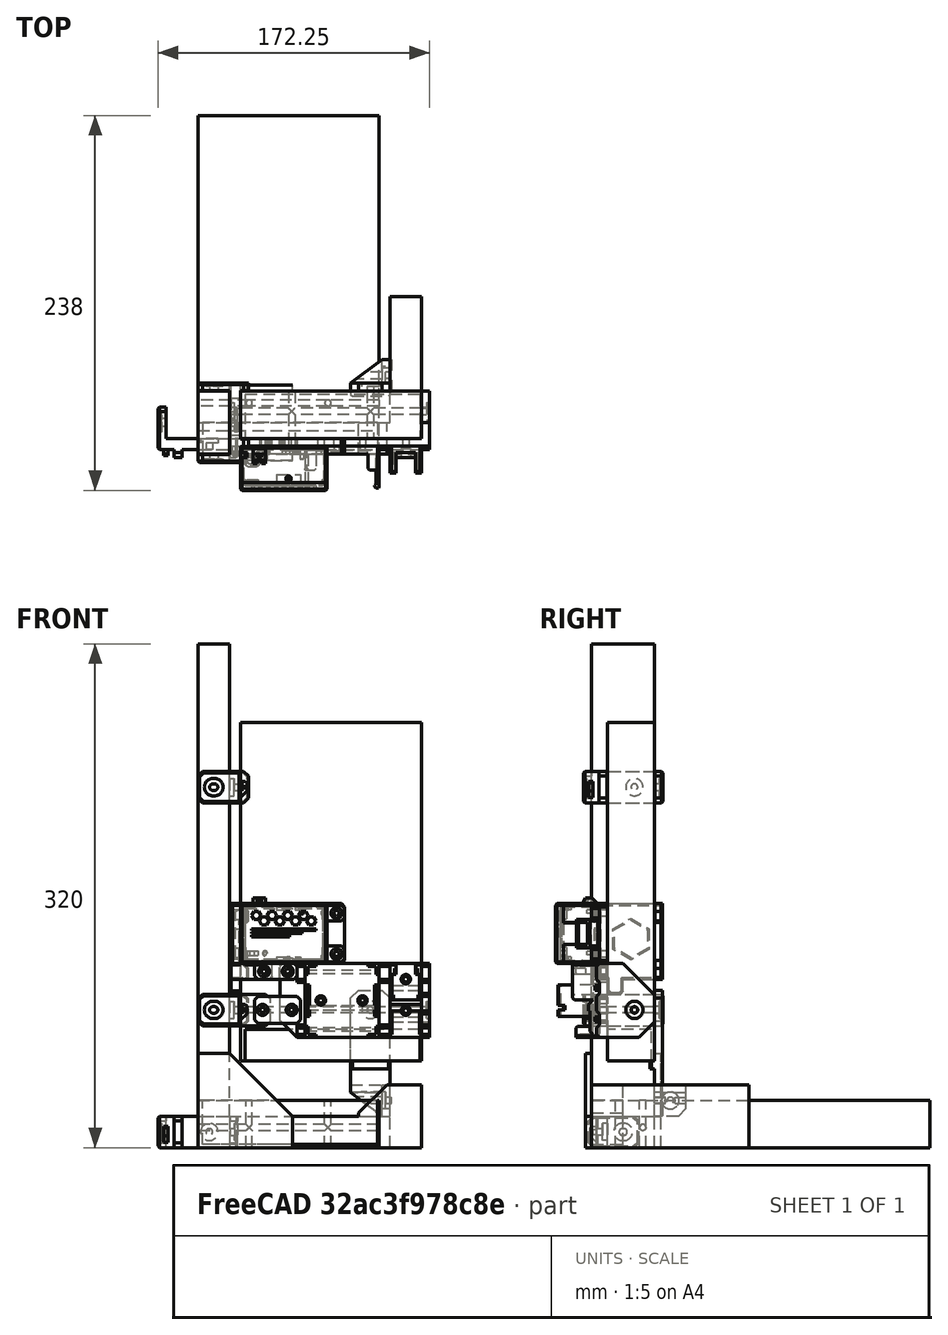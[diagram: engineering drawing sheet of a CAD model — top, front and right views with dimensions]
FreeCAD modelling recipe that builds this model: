
FCSTD DOCUMENT  (FreeCAD 0.18R16146 (Git))
Label: psu-aio-mount
License: All rights reserved
LicenseURL: http://en.wikipedia.org/wiki/All_rights_reserved
objects: Part::Box×50, Part::Chamfer×33, Part::Cylinder×32, Part::MultiFuse×30, Part::Feature×16, Part::Cut×16
note: 177 computed .brp shape members not serialized (recipe doc carries the construction recipe); baked Part::Feature solids carry a one-line shape summary decoded from their .brp

FEATURE [Part::Box] Box  label="Cube"
  AttacherType = Attacher::AttachEngine3D
  Height = 60
  Length = 60
  Width = 4
FEATURE [Part::Chamfer] Chamfer
  Base = -> Box
  Edges = 1 edges r=40: [Edge6]
  Placement = pos=(0,-4,0) rot=(0,0,1;0rad)
FEATURE [Part::Box] Box001  label="Cube001"
  AttacherType = Attacher::AttachEngine3D
  Height = 20
  Length = 122
  Width = 40
FEATURE [Part::Box] Box002  label="Cube002"
  AttacherType = Attacher::AttachEngine3D
  Height = 300
  Length = 20
  Placement = pos=(0,0,20) rot=(0,0,1;0rad)
  Width = 40
FEATURE [Part::Box] Box003  label="Cube003"
  AttacherType = Attacher::AttachEngine3D
  Height = 40
  Length = 20
  Placement = pos=(122,0,0) rot=(0,0,1;0rad)
  Width = 100
FEATURE [Part::Feature] Chamfer001
  Placement = pos=(0,40,0) rot=(0,0,1;0rad)
  shape: bbox 60 x 4 x 60 mm, 7 faces (baked)
FEATURE [Part::Box] Box004  label="Cube004"
  AttacherType = Attacher::AttachEngine3D
  Height = 20
  Length = 20
  Placement = pos=(102,0,20) rot=(0,0,1;0rad)
  Width = 20
FEATURE [Part::Chamfer] Chamfer002
  Base = -> Box004
  Edges = 1 edges r=18: [Edge2]
FEATURE [Part::MultiFuse] Fusion  label="Frame-pred"
  Shapes = -> [Chamfer002,Box001,Chamfer001,Box003,Box002,Chamfer]
FEATURE [Part::Feature] Cut002001  label="PSU-pref"
  Placement = pos=(142,40,55) rot=(0.57735,-0.57735,0.57735;2.0944rad)
  shape: bbox 115 x 30 x 215 mm, 17 faces (baked)
FEATURE [Part::Feature] Cut001001  label="sonoff-mounter001"
  Placement = pos=(130,8,117) rot=(0.57735,0.57735,-0.57735;2.0944rad)
  shape: bbox 47 x 26.5 x 47 mm, 92 faces (baked)
FEATURE [Part::Feature] Chamfer003001001  label="plug-holder-2-pin"
  Placement = pos=(122,5,117) rot=(0.57735,0.57735,-0.57735;2.0944rad)
  shape: bbox 20 x 17 x 47 mm, 63 faces (baked)
FEATURE [Part::Box] Box006  label="Cube006"
  AttacherType = Attacher::AttachEngine3D
  Height = 20
  Length = 40.5
  Placement = pos=(-20.25,3,0) rot=(0,0,1;0rad)
  Width = 7
FEATURE [Part::Box] Box007  label="Cube007"
  AttacherType = Attacher::AttachEngine3D
  Height = 20
  Length = 5
  Placement = pos=(-25.25,3,0) rot=(0,0,1;0rad)
  Width = 27
FEATURE [Part::Box] Box008  label="Cube008"
  AttacherType = Attacher::AttachEngine3D
  Height = 20
  Length = 5
  Placement = pos=(20.25,3,0) rot=(0,0,1;0rad)
  Width = 27
FEATURE [Part::Box] Box009  label="Cube009"
  AttacherType = Attacher::AttachEngine3D
  Height = 20
  Length = 5
  Placement = pos=(20.25,-2,0) rot=(0,0,1;0rad)
  Width = 5
FEATURE [Part::Box] Box010  label="Cube010"
  AttacherType = Attacher::AttachEngine3D
  Height = 20
  Length = 5
  Placement = pos=(-15.25,-2,0) rot=(0,0,1;0rad)
  Width = 5
FEATURE [Part::Cylinder] Cylinder
  Angle = 360
  AttacherType = Attacher::AttachEngine3D
  Height = 10
  Placement = pos=(7.2,11,10) rot=(1,0,0;1.5708rad)
  Radius = 2.1
FEATURE [Part::Cylinder] Cylinder001
  Angle = 360
  AttacherType = Attacher::AttachEngine3D
  Height = 10
  Placement = pos=(-20,20,10) rot=(0,-1,0;1.5708rad)
  Radius = 2.1
FEATURE [Part::Cylinder] Cylinder002
  Angle = 360
  AttacherType = Attacher::AttachEngine3D
  Height = 10
  Placement = pos=(30,20,10) rot=(0,-1,0;1.5708rad)
  Radius = 2.1
FEATURE [Part::Cylinder] Cylinder003
  Angle = 360
  AttacherType = Attacher::AttachEngine3D
  Height = 3
  Placement = pos=(7.2,10,10) rot=(1,0,0;1.5708rad)
  Radius = 5.5
FEATURE [Part::MultiFuse] Fusion001
  Shapes = -> [Cylinder003,Cylinder]
FEATURE [Part::Cylinder] Cylinder004
  Angle = 360
  AttacherType = Attacher::AttachEngine3D
  Height = 2
  Placement = pos=(25.25,20,10) rot=(0,-1,0;1.5708rad)
  Radius = 5.5
FEATURE [Part::MultiFuse] Fusion002
  Shapes = -> [Cylinder004,Cylinder002]
FEATURE [Part::Cylinder] Cylinder005
  Angle = 360
  AttacherType = Attacher::AttachEngine3D
  Height = 2
  Placement = pos=(-23.25,20,10) rot=(0,-1,0;1.5708rad)
  Radius = 5.5
FEATURE [Part::MultiFuse] Fusion003
  Shapes = -> [Cylinder005,Cylinder001]
FEATURE [Part::MultiFuse] Fusion004
  Shapes = -> [Box010,Box008,Box007,Box006,Box009]
FEATURE [Part::Feature] Fusion003001  label="Fusion005"
  Placement = pos=(0,1,0) rot=(0,0,1;0rad)
  shape: bbox 10 x 11 x 11 mm, 7 faces (baked)
FEATURE [Part::Feature] Fusion002001  label="Fusion006"
  Placement = pos=(0,1,0) rot=(0,0,1;0rad)
  shape: bbox 10 x 11 x 11 mm, 7 faces (baked)
FEATURE [Part::Box] Box011  label="Cube011"
  AttacherType = Attacher::AttachEngine3D
  Height = 4.2
  Length = 9
  Placement = pos=(-26,20,7.9) rot=(0,0,1;0rad)
  Width = 1
FEATURE [Part::Box] Box012  label="Cube012"
  AttacherType = Attacher::AttachEngine3D
  Height = 4.2
  Length = 9
  Placement = pos=(19,20,7.9) rot=(0,0,1;0rad)
  Width = 1
FEATURE [Part::Box] Box013  label="Cube013"
  AttacherType = Attacher::AttachEngine3D
  Height = 11
  Length = 2
  Placement = pos=(-25.25,20,4.5) rot=(0,0,1;0rad)
  Width = 1
FEATURE [Part::Box] Box014  label="Cube014"
  AttacherType = Attacher::AttachEngine3D
  Height = 11
  Length = 2
  Placement = pos=(23.25,20,4.5) rot=(0,0,1;0rad)
  Width = 1
FEATURE [Part::MultiFuse] Fusion003002
  Placement = pos=(0,-0.5,0) rot=(0,0,1;0rad)
  Shapes = -> [Box013,Box014,Box012,Box011,Fusion002001,Fusion003001,Fusion002,Fusion003]
FEATURE [Part::Cut] Cut
  Base = -> Fusion004
  Tool = -> Fusion003002
FEATURE [Part::Cut] Cut003023001003
  Base = -> Cut
  Tool = -> Fusion001
FEATURE [Part::Chamfer] Chamfer003001002
  Base = -> Cut003023001003
  Edges = 8 edges r=3: [Edge14,Edge18,Edge54,Edge57,Edge69,Edge75,Edge80,Edge93]
FEATURE [Part::Box] Box015  label="Cube015"
  AttacherType = Attacher::AttachEngine3D
  Height = 3
  Length = 3
  Placement = pos=(-22,1,8.5) rot=(0,0,1;0rad)
  Width = 3
FEATURE [Part::Box] Box016  label="Cube016"
  AttacherType = Attacher::AttachEngine3D
  Height = 10
  Length = 3
  Placement = pos=(-22,-1,3.5) rot=(0,0,1;0rad)
  Width = 5
FEATURE [Part::Chamfer] Chamfer003001003
  Base = -> Box016
  Edges = 1 edges r=4: [Edge9]
FEATURE [Part::Cut] Cut003023001004
  Base = -> Chamfer003001003
  Tool = -> Box015
FEATURE [Part::Chamfer] Chamfer003001004
  Base = -> Cut003023001004
  Edges = 1 edges r=1: [Edge12]
FEATURE [Part::MultiFuse] Fusion003003
  Shapes = -> [Chamfer003001002,Chamfer003001004]
FEATURE [Part::Chamfer] Chamfer003001005  label="PSU-mounter"
  Base = -> Fusion003003
  Edges = 16 edges r=1: [Edge13,Edge16,Edge21,Edge25,Edge27,Edge47,Edge65,Edge76,Edge95,Edge96,Edge97,Edge110,Edge116,Edge119,Edge120,Edge139]
FEATURE [Part::Box] Box017  label="Cube017"
  AttacherType = Attacher::AttachEngine3D
  Height = 30
  Length = 115
  Placement = pos=(0,15,0) rot=(0,0,1;0rad)
  Width = 5
FEATURE [Part::Cylinder] Cylinder006
  Angle = 360
  AttacherType = Attacher::AttachEngine3D
  Height = 41
  Placement = pos=(32.5,32.5,0) rot=(0,0,1;0rad)
  Radius = 2.1
FEATURE [Part::Box] Box018  label="Cube018"
  AttacherType = Attacher::AttachEngine3D
  Height = 5
  Length = 95
  Placement = pos=(25,15,30) rot=(0,0,1;0rad)
  Width = 47
FEATURE [Part::Box] Box019  label="Cube019"
  AttacherType = Attacher::AttachEngine3D
  Height = 35
  Length = 5
  Placement = pos=(115,15,0) rot=(0,0,1;0rad)
  Width = 47
FEATURE [Part::Box] Box020  label="Cube020"
  AttacherType = Attacher::AttachEngine3D
  Height = 3
  Length = 5
  Placement = pos=(115,15,35) rot=(0,0,1;0rad)
  Width = 8
FEATURE [Part::Box] Box021  label="Cube021"
  AttacherType = Attacher::AttachEngine3D
  Height = 3
  Length = 5
  Placement = pos=(115,30,35) rot=(0,0,1;0rad)
  Width = 13
FEATURE [Part::Box] Box022  label="Cube022"
  AttacherType = Attacher::AttachEngine3D
  Height = 3
  Length = 5
  Placement = pos=(115,50,35) rot=(0,0,1;0rad)
  Width = 12
FEATURE [Part::Box] Box023  label="Cube023"
  AttacherType = Attacher::AttachEngine3D
  Height = 3
  Length = 7
  Placement = pos=(88,15,35) rot=(0,0,1;0rad)
  Width = 8
FEATURE [Part::Box] Box024  label="Cube024"
  AttacherType = Attacher::AttachEngine3D
  Height = 3
  Length = 7
  Placement = pos=(88,50,35) rot=(0,0,1;0rad)
  Width = 12
FEATURE [Part::Box] Box025  label="Cube025"
  AttacherType = Attacher::AttachEngine3D
  Height = 3
  Length = 5
  Placement = pos=(36,50,35) rot=(0,0,1;0rad)
  Width = 12
FEATURE [Part::Box] Box026  label="Cube026"
  AttacherType = Attacher::AttachEngine3D
  Height = 3
  Length = 5
  Placement = pos=(36,15,35) rot=(0,0,1;0rad)
  Width = 8
FEATURE [Part::MultiFuse] Fusion003004
  Placement = pos=(0,0,-1) rot=(0,0,1;0rad)
  Shapes = -> [Box020,Box021,Box022,Box023,Box024,Box025,Box026]
FEATURE [Part::Chamfer] Chamfer003001007
  Base = -> Fusion003004
  Edges = 14 edges r=2: [Edge10,Edge12,Edge22,Edge24,Edge34,Edge36,Edge46,Edge48,Edge58,Edge60,Edge70,Edge72,Edge82,Edge84]
FEATURE [Part::Cylinder] Cylinder007
  Angle = 360
  AttacherType = Attacher::AttachEngine3D
  Height = 3
  Placement = pos=(32.5,32.5,32) rot=(0,0,1;0rad)
  Radius = 5.5
FEATURE [Part::MultiFuse] Fusion003005
  Shapes = -> [Box018,Box019,Chamfer003001007]
FEATURE [Part::Cylinder] Cylinder008
  Angle = 360
  AttacherType = Attacher::AttachEngine3D
  Height = 10
  Placement = pos=(114,32.5,12.8) rot=(0,1,0;1.5708rad)
  Radius = 2.1
FEATURE [Part::Cylinder] Cylinder009
  Angle = 360
  AttacherType = Attacher::AttachEngine3D
  Height = 2
  Placement = pos=(118,32.5,12.8) rot=(0,1,0;1.5708rad)
  Radius = 5.5
FEATURE [Part::MultiFuse] Fusion003007
  Shapes = -> [Cylinder009,Cylinder008]
FEATURE [Part::MultiFuse] Fusion003008
  Shapes = -> [Cylinder006,Cylinder007]
FEATURE [Part::MultiFuse] Fusion003009
  Shapes = -> [Fusion003007,Fusion003008]
FEATURE [Part::Cut] Cut003023001006
  Base = -> Fusion003005
  Tool = -> Fusion003009
FEATURE [Part::Chamfer] Chamfer003001008
  Base = -> Cut003023001006
  Edges = 1 edges r=10: [Edge115]
FEATURE [Part::Chamfer] Chamfer003001009
  Base = -> Chamfer003001008
  Edges = 1 edges r=20: [Edge16]
FEATURE [Part::Chamfer] Chamfer003001010
  Base = -> Chamfer003001009
  Edges = 1 edges r=10.99: [Edge44]
FEATURE [Part::Cylinder] Cylinder010
  Angle = 360
  AttacherType = Attacher::AttachEngine3D
  Height = 10
  Placement = pos=(51,38.5,29) rot=(0,0,1;0rad)
  Radius = 2.05
FEATURE [Part::Cylinder] Cylinder011
  Angle = 360
  AttacherType = Attacher::AttachEngine3D
  Height = 10
  Placement = pos=(77.5,38.5,29) rot=(0,0,1;0rad)
  Radius = 2.05
FEATURE [Part::Cylinder] Cylinder012
  Angle = 360
  AttacherType = Attacher::AttachEngine3D
  Height = 10
  Placement = pos=(105,52,29) rot=(0,0,1;0rad)
  Radius = 2.05
FEATURE [Part::Cylinder] Cylinder013
  Angle = 360
  AttacherType = Attacher::AttachEngine3D
  Height = 10
  Placement = pos=(105,32,29) rot=(0,0,1;0rad)
  Radius = 2.05
FEATURE [Part::MultiFuse] Fusion003010
  Shapes = -> [Cylinder013,Cylinder012,Cylinder011,Cylinder010]
FEATURE [Part::Cut] Cut003023001007
  Base = -> Chamfer003001010
  Tool = -> Fusion003010
FEATURE [Part::Cylinder] Cylinder014
  Angle = 360
  AttacherType = Attacher::AttachEngine3D
  Height = 10
  Placement = pos=(30,57,26.5) rot=(0,0,1;0rad)
  Radius = 2.1
FEATURE [Part::Chamfer] Chamfer003001011
  Base = -> Cut003023001007
  Edges = 1 edges r=2: [Edge13]
FEATURE [Part::Cut] Cut003023001008
  Base = -> Chamfer003001011
  Placement = pos=(27,40,55) rot=(1,0,0;1.5708rad)
  Tool = -> Cylinder014
FEATURE [Part::Feature] Chamfer003001005001  label="PSU-mounter001"
  Placement = pos=(30,20,77.5) rot=(0,0,1;1.5708rad)
  shape: bbox 32 x 50.5 x 20 mm, 102 faces (baked)
FEATURE [Part::Feature] Chamfer003001005002  label="PSU-mounter002"
  Placement = pos=(30,20,219) rot=(0,0,1;1.5708rad)
  shape: bbox 32 x 50.5 x 20 mm, 102 faces (baked)
FEATURE [Part::Feature] Cut002001001  label="PSU-pref001"
  Placement = pos=(115,-4e-15,-2.8e-14) rot=(0,0,1;1.5708rad)
  shape: bbox 115 x 215 x 30 mm, 17 faces (baked)
FEATURE [Part::Box] Box027  label="Cube027"
  AttacherType = Attacher::AttachEngine3D
  Height = 3
  Length = 25
  Placement = pos=(70,-5,0) rot=(0,0,1;0rad)
  Width = 5
FEATURE [Part::Cylinder] Cylinder015
  Angle = 360
  AttacherType = Attacher::AttachEngine3D
  Height = 32
  Placement = pos=(82.5,32.5,-15) rot=(0,0,1;0rad)
  Radius = 2.1
FEATURE [Part::Box] Box028  label="Cube028"
  AttacherType = Attacher::AttachEngine3D
  Height = 5
  Length = 25
  Placement = pos=(70,-15,-5) rot=(0,0,1;0rad)
  Width = 60
FEATURE [Part::Box] Box029  label="Cube029"
  AttacherType = Attacher::AttachEngine3D
  Height = 20
  Length = 5
  Placement = pos=(90,-35,-20) rot=(0,0,1;0rad)
  Width = 20
FEATURE [Part::Box] Box030  label="Cube030"
  AttacherType = Attacher::AttachEngine3D
  Height = 20
  Length = 25
  Placement = pos=(70,-20,-20) rot=(0,0,1;0rad)
  Width = 5
FEATURE [Part::Cylinder] Cylinder016
  Angle = 360
  AttacherType = Attacher::AttachEngine3D
  Height = 25
  Placement = pos=(95,-25,-10) rot=(0,-1,0;1.5708rad)
  Radius = 2.1
FEATURE [Part::Cylinder] Cylinder017
  Angle = 360
  AttacherType = Attacher::AttachEngine3D
  Height = 22
  Placement = pos=(92,-25,-10) rot=(0,-1,0;1.5708rad)
  Radius = 5.5
FEATURE [Part::MultiFuse] Fusion003011
  Shapes = -> [Cylinder017,Cylinder016]
FEATURE [Part::Box] Box031  label="Cube031"
  AttacherType = Attacher::AttachEngine3D
  Height = 5
  Length = 25
  Placement = pos=(70,-35,-5) rot=(0,0,1;0rad)
  Width = 20
FEATURE [Part::Chamfer] Chamfer003001005003
  Base = -> Box030
  Edges = 1 edges: [Edge4 r1=15 r2=20]
FEATURE [Part::Chamfer] Chamfer003001005004
  Base = -> Box031
  Edges = 1 edges: [Edge1 r1=15 r2=20]
FEATURE [Part::Box] Box032  label="Cube032"
  AttacherType = Attacher::AttachEngine3D
  Height = 7
  Length = 2
  Placement = pos=(94,-27,-20) rot=(0,0,1;0rad)
  Width = 4
FEATURE [Part::Box] Box033  label="Cube033"
  AttacherType = Attacher::AttachEngine3D
  Height = 7
  Length = 2
  Placement = pos=(94,-27,-7) rot=(0,0,1;0rad)
  Width = 4
FEATURE [Part::MultiFuse] Fusion003012
  Shapes = -> [Box033,Box032,Chamfer003001005004,Chamfer003001005003,Box029,Box028,Box027]
FEATURE [Part::Chamfer] Chamfer003001005005
  Base = -> Fusion003012
  Edges = 2 edges r=1: [Edge85,Edge92]
FEATURE [Part::Chamfer] Chamfer003001005006
  Base = -> Chamfer003001005005
  Edges = 1 edges r=5: [Edge90]
FEATURE [Part::Cut] Cut003023001009
  Base = -> Chamfer003001005006
  Tool = -> Fusion003011
FEATURE [Part::Chamfer] Chamfer003001005007
  Base = -> Cut003023001009
  Edges = 2 edges r=5: [Edge94,Edge113]
FEATURE [Part::Cylinder] Cylinder018
  Angle = 360
  AttacherType = Attacher::AttachEngine3D
  Height = 2
  Placement = pos=(82.5,32.5,-5) rot=(0,0,1;0rad)
  Radius = 5.5
FEATURE [Part::MultiFuse] Fusion003013
  Shapes = -> [Cylinder018,Cylinder015]
FEATURE [Part::Cut] Cut003023001010  label="psu-supporter"
  Base = -> Chamfer003001005007
  Placement = pos=(27,40,55) rot=(1,0,0;1.5708rad)
  Tool = -> Fusion003013
FEATURE [Part::Box] Box034  label="Cube034"
  AttacherType = Attacher::AttachEngine3D
  Height = 20.3
  Length = 18.15
  Placement = pos=(28,4.75,77.85) rot=(0,0,1;0rad)
  Width = 5
FEATURE [Part::Box] Box035  label="Cube035"
  AttacherType = Attacher::AttachEngine3D
  Height = 13
  Length = 13
  Placement = pos=(53,5,81) rot=(0,0,1;0rad)
  Width = 5
FEATURE [Part::MultiFuse] Fusion003015
  Shapes = -> [Cut003023001008,Box035]
FEATURE [Part::Cylinder] Cylinder019
  Angle = 360
  AttacherType = Attacher::AttachEngine3D
  Height = 10
  Placement = pos=(59.5,11,87.5) rot=(1,0,0;1.5708rad)
  Radius = 2.05
FEATURE [Part::Cylinder] Cylinder020
  Angle = 360
  AttacherType = Attacher::AttachEngine3D
  Height = 10
  Placement = pos=(41,10,87.5) rot=(1,0,0;1.5708rad)
  Radius = 2.05
FEATURE [Part::Box] Box036  label="Cube036"
  AttacherType = Attacher::AttachEngine3D
  Height = 20
  Length = 18
  Placement = pos=(28,4.75,78) rot=(0,0,1;0rad)
  Width = 5
FEATURE [Part::Chamfer] Chamfer003001005008
  Base = -> Box036
  Edges = 2 edges r=3: [Edge6,Edge8]
  Placement = pos=(0,0,-0.5) rot=(0,0,1;0rad)
FEATURE [Part::Cut] Cut003023001012  label="block-mount"
  Base = -> Fusion003015
  Tool = -> Cylinder019
FEATURE [Part::Chamfer] Chamfer003001005009  label="cutout-1"
  Base = -> Box034
  Edges = 2 edges r=3: [Edge6,Edge8]
  Placement = pos=(0,0,-0.5) rot=(0,0,1;0rad)
FEATURE [Part::Box] Box037  label="Cube037"
  AttacherType = Attacher::AttachEngine3D
  Height = 28
  Length = 18
  Placement = pos=(51.85,5,78) rot=(0,0,1;0rad)
  Width = 5
FEATURE [Part::Chamfer] Chamfer003001005012
  Base = -> Box037
  Edges = 1 edges r=2.99: [Edge4]
FEATURE [Part::Cylinder] Cylinder021
  Angle = 360
  AttacherType = Attacher::AttachEngine3D
  Height = 10
  Placement = pos=(41,1.9e-14,87.5) rot=(-1,0,0;1.5708rad)
  Radius = 1.65
FEATURE [Part::Cylinder] Cylinder022
  Angle = 360
  AttacherType = Attacher::AttachEngine3D
  Height = 10
  Placement = pos=(59.5,1.9e-14,87.5) rot=(-1,0,0;1.5708rad)
  Radius = 1.65
FEATURE [Part::Cylinder] Cylinder023
  Angle = 360
  AttacherType = Attacher::AttachEngine3D
  Height = 2
  Placement = pos=(59.5,1.9e-14,87.5) rot=(-1,0,0;1.5708rad)
  Radius = 3.5
FEATURE [Part::Cylinder] Cylinder024
  Angle = 360
  AttacherType = Attacher::AttachEngine3D
  Height = 2
  Placement = pos=(41,1.9e-14,87.5) rot=(-1,0,0;1.5708rad)
  Radius = 3.5
FEATURE [Part::MultiFuse] Fusion003018
  Shapes = -> [Cylinder022,Cylinder021]
FEATURE [Part::MultiFuse] Fusion003019
  Shapes = -> [Cylinder024,Cylinder023]
FEATURE [Part::Feature] Chamfer002001  label="acdc-cap"
  Placement = pos=(29,5,153) rot=(0.57735,0.57735,-0.57735;2.0944rad)
  shape: bbox 55 x 14.5 x 38 mm, 137 faces (baked)
FEATURE [Part::Feature] Cut003023001016  label="acdc-bolt-hole001"
  Placement = pos=(88,5,149) rot=(0.57735,-0.57735,0.57735;2.0944rad)
  shape: bbox 12 x 5 x 10 mm, 11 faces (baked)
FEATURE [Part::Feature] Cut003023001017  label="acdc-bolt-hole002"
  Placement = pos=(88,5,123) rot=(0.57735,-0.57735,0.57735;2.0944rad)
  shape: bbox 12 x 5 x 10 mm, 11 faces (baked)
FEATURE [Part::Feature] Part__Feature001  label="zip-tie-slot"
  Placement = pos=(43.4667,3.64686,155) rot=(0,0,1;3.14159rad)
  shape: bbox 8 x 9.5 x 3.5 mm, 30 faces (baked)
FEATURE [Part::Box] Box039  label="Cube039"
  AttacherType = Attacher::AttachEngine3D
  Height = 48
  Length = 7
  Placement = pos=(20,5,107) rot=(0,0,1;0rad)
  Width = 40
FEATURE [Part::Box] Box040  label="Cube040"
  AttacherType = Attacher::AttachEngine3D
  Height = 10
  Length = 27
  Placement = pos=(20,5,107) rot=(0,0,1;0rad)
  Width = 5
FEATURE [Part::Box] Box041  label="Cube041"
  AttacherType = Attacher::AttachEngine3D
  Height = 38
  Length = 73
  Placement = pos=(20,5,117) rot=(0,0,1;0rad)
  Width = 5
FEATURE [Part::Box] Box042  label="Cube042"
  AttacherType = Attacher::AttachEngine3D
  Height = 12
  Length = 12
  Placement = pos=(20,40.15,98) rot=(0,0,1;0rad)
  Width = 4.85
FEATURE [Part::Box] Box043  label="Cube043"
  AttacherType = Attacher::AttachEngine3D
  Height = 12
  Length = 12
  Placement = pos=(20,40.15,143) rot=(0,0,1;0rad)
  Width = 4.85
FEATURE [Part::Chamfer] Chamfer003001005020
  Base = -> Box041
  Edges = 2 edges r=2: [Edge6,Edge8]
FEATURE [Part::Cylinder] Cylinder026
  Angle = 360
  AttacherType = Attacher::AttachEngine3D
  Height = 10
  Placement = pos=(88,2.72e-14,123) rot=(1,0,0;1.5708rad)
  Radius = 2.05
FEATURE [Part::Cylinder] Cylinder027
  Angle = 360
  AttacherType = Attacher::AttachEngine3D
  Height = 10
  Placement = pos=(88,3.28e-14,149) rot=(1,0,0;1.5708rad)
  Radius = 2.05
FEATURE [Part::Cylinder] Cylinder028
  Angle = 360
  AttacherType = Attacher::AttachEngine3D
  Height = 10
  Placement = pos=(42,2.5e-14,112) rot=(1,0,0;1.5708rad)
  Radius = 2.05
FEATURE [Part::Box] Box044  label="Cube044"
  AttacherType = Attacher::AttachEngine3D
  Height = 31.4
  Length = 5
  Placement = pos=(22,1.85,119.8) rot=(0,0,1;0rad)
  Width = 3.15
FEATURE [Part::Chamfer] Chamfer003001005025
  Base = -> Box042
  Edges = 1 edges r=5: [Edge6]
FEATURE [Part::Chamfer] Chamfer003001005026
  Base = -> Box043
  Edges = 1 edges r=5: [Edge6]
FEATURE [Part::Chamfer] Chamfer003001005027
  Base = -> Chamfer003001005025
  Edges = 1 edges r=1: [Edge3]
  Placement = pos=(0,0,9) rot=(0,0,1;0rad)
FEATURE [Part::Chamfer] Chamfer003001005028
  Base = -> Chamfer003001005026
  Edges = 1 edges r=1: [Edge3]
FEATURE [Part::Box] Box046  label="Cube046"
  AttacherType = Attacher::AttachEngine3D
  Height = 31
  Length = 4
  Placement = pos=(24,2,120) rot=(0,0,1;0rad)
  Width = 3
FEATURE [Part::Chamfer] Chamfer003001005030
  Base = -> Box046
  Edges = 2 edges r=1: [Edge2,Edge4]
FEATURE [Part::Box] Box047  label="Cube047"
  AttacherType = Attacher::AttachEngine3D
  Height = 39
  Length = 5
  Placement = pos=(22,-1,116) rot=(0,0,1;0rad)
  Width = 6
FEATURE [Part::Cut] Cut003023001020
  Base = -> Box047
  Tool = -> Box044
FEATURE [Part::Chamfer] Chamfer003001005031
  Base = -> Cut003023001020
  Edges = 2 edges r=1: [Edge11,Edge23]
FEATURE [Part::MultiFuse] Fusion003023003
  Placement = pos=(0,12,0) rot=(0,0,1;0rad)
  Shapes = -> [Cylinder026,Cylinder027,Cylinder028]
FEATURE [Part::Box] Box048  label="Cube048"
  AttacherType = Attacher::AttachEngine3D
  Height = 9.5
  Length = 7
  Placement = pos=(20,10,97.5) rot=(0,0,1;0rad)
  Width = 10
FEATURE [Part::Cut] Cut003023001021
  Base = -> Chamfer003001005008
  Tool = -> Cylinder020
FEATURE [Part::MultiFuse] Fusion003023004  label="psu-mount-btm-f1"
  Shapes = -> [Chamfer003001005001,Cut003023001021]
FEATURE [Part::MultiFuse] Fusion003023005
  Shapes = -> [Chamfer003001005012,Chamfer003001005009]
FEATURE [Part::Box] Box049  label="Cube049"
  AttacherType = Attacher::AttachEngine3D
  Height = 17
  Length = 29
  Placement = pos=(36,0,79) rot=(0,0,1;0rad)
  Width = 9.5
FEATURE [Part::Chamfer] Chamfer003001005032
  Base = -> Box049
  Edges = 4 edges r=2: [Edge2,Edge4,Edge6,Edge8]
FEATURE [Part::Cut] Cut003023001022
  Base = -> Chamfer003001005032
  Tool = -> Fusion003023005
FEATURE [Part::MultiFuse] Fusion003023006
  Shapes = -> [Fusion003019,Fusion003018]
FEATURE [Part::Cut] Cut003023001023  label="mount-connector-lower-f1"
  Base = -> Cut003023001022
  Tool = -> Fusion003023006
FEATURE [Part::Chamfer] Chamfer003001005033
  Base = -> Box040
  Edges = 1 edges r=2: [Edge8]
FEATURE [Part::Chamfer] Chamfer003001005034
  Base = -> Box048
  Edges = 2 edges r=2: [Edge9,Edge11]
FEATURE [Part::MultiFuse] Fusion003023007
  Shapes = -> [Chamfer003001005034,Chamfer003001005033,Chamfer003001005031,Chamfer003001005020,Box039,Chamfer003001005027,Chamfer003001005028]
FEATURE [Part::Cylinder] Cylinder029
  Angle = 360
  AttacherType = Attacher::AttachEngine3D
  Height = 13
  Placement = pos=(42,10,112) rot=(1,0,0;1.5708rad)
  Radius = 1.65
FEATURE [Part::Cylinder] Cylinder030
  Angle = 360
  AttacherType = Attacher::AttachEngine3D
  Height = 13
  Placement = pos=(57,10,112) rot=(1,0,0;1.5708rad)
  Radius = 1.65
FEATURE [Part::Box] Box050  label="Cube050"
  AttacherType = Attacher::AttachEngine3D
  Height = 10
  Length = 27
  Placement = pos=(36,0,107) rot=(0,0,1;0rad)
  Width = 9.5
FEATURE [Part::Box] Box051  label="Cube051"
  AttacherType = Attacher::AttachEngine3D
  Height = 10.15
  Length = 11.15
  Placement = pos=(36,5,106.85) rot=(0,0,1;0rad)
  Width = 5
FEATURE [Part::Chamfer] Chamfer003001005036
  Base = -> Box050
  Edges = 4 edges r=2: [Edge2,Edge4,Edge6,Edge8]
FEATURE [Part::Box] Box052  label="Cube052"
  AttacherType = Attacher::AttachEngine3D
  Height = 10
  Length = 11
  Placement = pos=(51.85,5,107) rot=(0,0,1;0rad)
  Width = 5
FEATURE [Part::Chamfer] Chamfer003001005037
  Base = -> Box051
  Edges = 1 edges r=2: [Edge8]
FEATURE [Part::Chamfer] Chamfer003001005038
  Base = -> Box052
  Edges = 1 edges r=2: [Edge2]
FEATURE [Part::MultiFuse] Fusion003023008
  Shapes = -> [Chamfer003001005037,Chamfer003001005038]
FEATURE [Part::Cut] Cut003023001024002
  Base = -> Chamfer003001005036
  Tool = -> Fusion003023008
FEATURE [Part::Cylinder] Cylinder031
  Angle = 360
  AttacherType = Attacher::AttachEngine3D
  Height = 2
  Placement = pos=(57,10,112) rot=(1,0,0;1.5708rad)
  Radius = 3.5
FEATURE [Part::Cylinder] Cylinder032
  Angle = 360
  AttacherType = Attacher::AttachEngine3D
  Height = 2
  Placement = pos=(42,10,112) rot=(1,0,0;1.5708rad)
  Radius = 3.5
FEATURE [Part::MultiFuse] Fusion003023009
  Placement = pos=(0,-8,0) rot=(0,0,1;0rad)
  Shapes = -> [Cylinder031,Cylinder032]
FEATURE [Part::MultiFuse] Fusion003023010
  Shapes = -> [Cylinder029,Cylinder030]
FEATURE [Part::MultiFuse] Fusion003023011
  Shapes = -> [Fusion003023009,Fusion003023010]
FEATURE [Part::Cut] Cut003023001024003  label="mount-connector-top"
  Base = -> Cut003023001024002
  Tool = -> Fusion003023011
FEATURE [Part::Feature] Body001001  label="Body002"
  Placement = pos=(29,25,132.5) rot=(0,0,1;0rad)
  shape: bbox 10 x 20.78 x 24 mm, 8 faces (baked)
FEATURE [Part::MultiFuse] Fusion003023012
  Shapes = -> [Fusion003023003,Body001001]
FEATURE [Part::Cut] Cut003023001024004  label="acdc-mount-base"
  Base = -> Fusion003023007
  Tool = -> Fusion003023012
FEATURE [Part::Feature] Cut003023001024004001  label="acdc-mount-base001"
  shape: bbox 73 x 46 x 57.5 mm, 46 faces (baked)
FEATURE [Part::Chamfer] Chamfer003001005039  label="acdc-mount-refine"
  Base = -> Cut003023001024004001
  Edges = 26 edges r=1: [Edge8,Edge10,Edge12,Edge13,Edge14,Edge19,Edge20,Edge26,Edge27,Edge30,Edge35,Edge59,Edge95,Edge96,Edge97,Edge98,Edge99,Edge100,Edge101,Edge102,Edge117,Edge125,Edge129,Edge131,Edge132,Edge133]
FEATURE [Part::Feature] Chamfer003003001  label="Chamfer003004"
  Placement = pos=(29,5,153) rot=(-0.57735,-0.57735,0.57735;4.18879rad)
  shape: bbox 55 x 23 x 39 mm, 89 faces (baked)
FEATURE [Part::MultiFuse] Fusion003023013
  Shapes = -> [Chamfer003001005030,Chamfer003003001,Part__Feature001,Cut003023001016,Cut003023001017]
